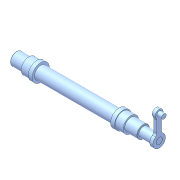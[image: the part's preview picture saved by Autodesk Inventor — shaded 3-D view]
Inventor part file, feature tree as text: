
AUTODESK INVENTOR PART (.ipt)
format: ipt  version: unknown  size: 248,320 bytes
history: native  units: in
note: dims shown in document units (in); Inventor stores cm internally (conversion verified against a paired STEP export)
features: sketch x7, extrude x6, chamfer x2, fillet x2, revolve x1, mirror x1
ambient origin geometry x8: Origin, YZ Plane, XZ Plane, XY Plane, X Axis, Y Axis, Z Axis, Center Point
feature tree (19):
  revolve  "Revolution1"  [1 undecoded]
  mirror  "Mirror1"
  extrude  "Extrusion14"  Depth=0.315in
  extrude  "Extrusion15"  Depth=0.3937in
  chamfer  "Chamfer3"  Distance=3.937in
  extrude  "Extrusion16"  Depth=0.7874in TaperAngle=0.0deg
  fillet  "Fillet1"  Radius=0.0197in
  chamfer  "Chamfer4"  Distance=0.1181in
  extrude  "Extrusion17"  Depth=0.0591in
  extrude  "Extrusion18"  Depth=0.1772in
  fillet  "Fillet2"  Radius=0.6299in
  extrude  "Extrusion19"  Depth=0.0591in
  sketch  "Sketch15"  dims[d21=0.7874in d66=0.3937in]
  sketch  "Sketch16"  dims[d67=0.4331in d68=0.315in]
  sketch  "Sketch17"  dims[d69=2.1654in d70=0.3937in]
  sketch  "Sketch18"  dims[d71=0.6299in]
  sketch  "Sketch19"  dims[d72=90.0deg]
  sketch  "Sketch20"  dims[d73=0.6299in d74=3.937in d75=0.0in]
  sketch  "Sketch21"  dims[d76=0.4724in d77=0.7874in d78=0.0in d79=0.0197in d80=0.0787in d81=45.0deg d82=0.1181in d83=0.0591in d84=0.1772in d85=0.6299in d86=0.0in d87=0.0591in d88=0.0197in d89=0.0787in d90=45.0deg d91=0.3937in d92=0.6299in d93=1.1811in d94=0.1181in d95=0.1575in d96=0.0in d97=0.315in d98=0.0039in d99=0.0in d100=0.1575in d101=0.2362in d102=0.2362in d103=0.0in]
note: 1 required parameter value undecoded (feature->parameter linkage not recoverable at this tier; creation-order binding heuristic only, values carry confidence <= 0.55)
